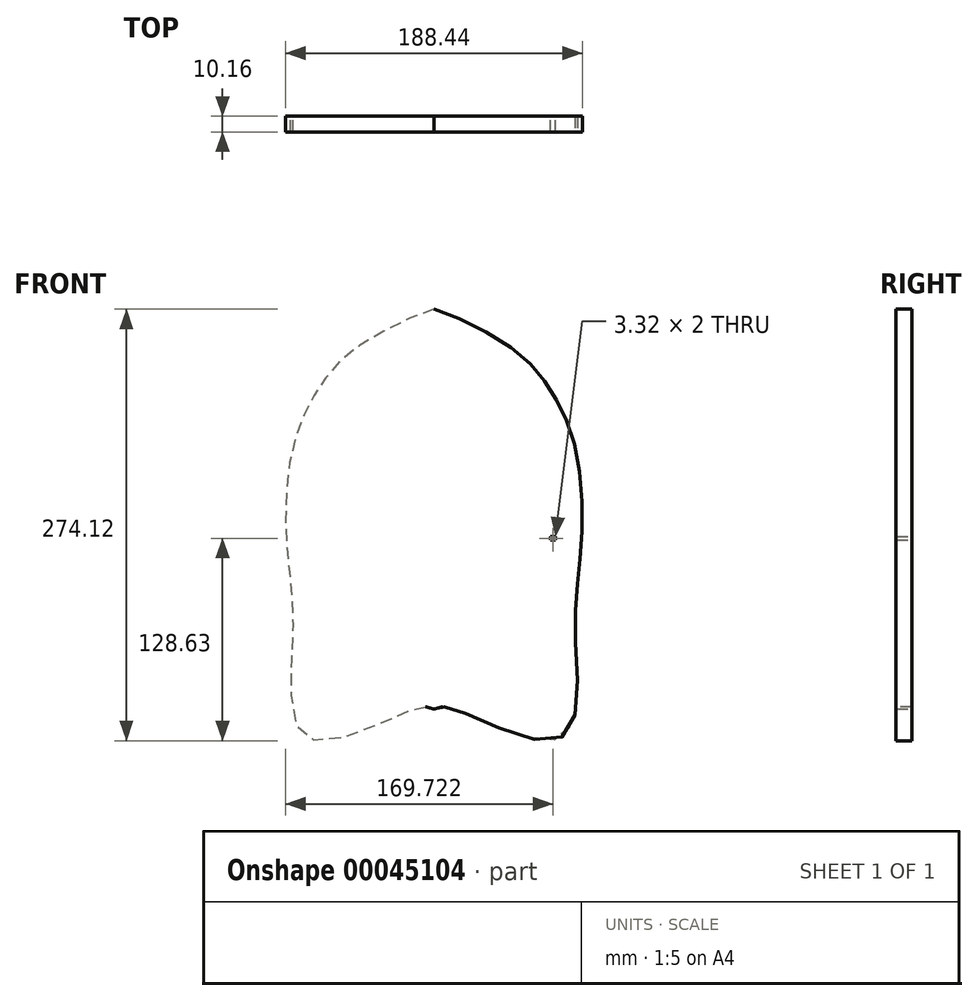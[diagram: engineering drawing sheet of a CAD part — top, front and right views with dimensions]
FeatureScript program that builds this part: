
annotation { "Feature Type Name" : "Feature", "Feature Type Description" : "" }
export const myFeature = defineFeature(function(context is Context, id is Id, definition is map)
    precondition{}
    {
        {
            var Q0;
            Q0=qCreatedBy(makeId("Front.planeOp"),FACE);
            var sketch = newSketch(context, id + "F0", { "sketchPlane" : qUnion([Q0])});
            skFitSpline(sketch, "E0", {"points": [v(0, 146.49) * mm, v(-51.23, 120.54) * mm, v(-75.75, 92.3) * mm, v(-90.74, 54.12) * mm, v(-93.37, -6.63) * mm, v(-89.64, -57.8) * mm, v(-79.38, -126.29) * mm, v(-9.41, -106.4) * mm, v(0, -107.51) * mm], "startDerivative": vector(-325.93, -101) * mm, "endDerivative": vector(191.24, -37.34) * mm});
            skFitSpline(sketch, "E1.MirrorCS", {"points": [v(0, 146.49) * mm, v(51.23, 120.54) * mm, v(75.75, 92.3) * mm, v(90.74, 54.12) * mm, v(93.37, -6.63) * mm, v(89.64, -57.8) * mm, v(79.38, -126.29) * mm, v(9.41, -106.4) * mm, v(0, -107.51) * mm], "startDerivative": vector(325.93, -101) * mm, "endDerivative": vector(-191.24, -37.34) * mm});
            skLineSegment(sketch, "E2.bottom", {"start": v(77.16, 0) * mm, "end": v(73.84, 0) * mm});
            skLineSegment(sketch, "E2.top", {"start": v(77.16, 2) * mm, "end": v(73.84, 2) * mm});
            skLineSegment(sketch, "E2.left", {"start": v(77.16, 0) * mm, "end": v(77.16, 2) * mm});
            skLineSegment(sketch, "E2.right", {"start": v(73.84, 0) * mm, "end": v(73.84, 2) * mm});
            skLineSegment(sketch, "E3.MirrorCS", {"start": v(70.52, 0) * mm, "end": v(73.84, 0) * mm});
            skSolve(sketch);
        }
        {
            var Q0;
            Q0=makeQuery(id+"F0.imprint","IMPRINT",FACE,{"disambiguationData":[TD([[makeQuery(id+"F0.imprint","IMPRINT",EDGE,{"derivedFrom":sQuery(id+"F0.wireOp",EDGE,"E0")}),1.0]])]});
            extrude(context, id + "F1", {"entities" : qUnion([Q0]), "depth" : 10.16 * mm});
        }
    });
